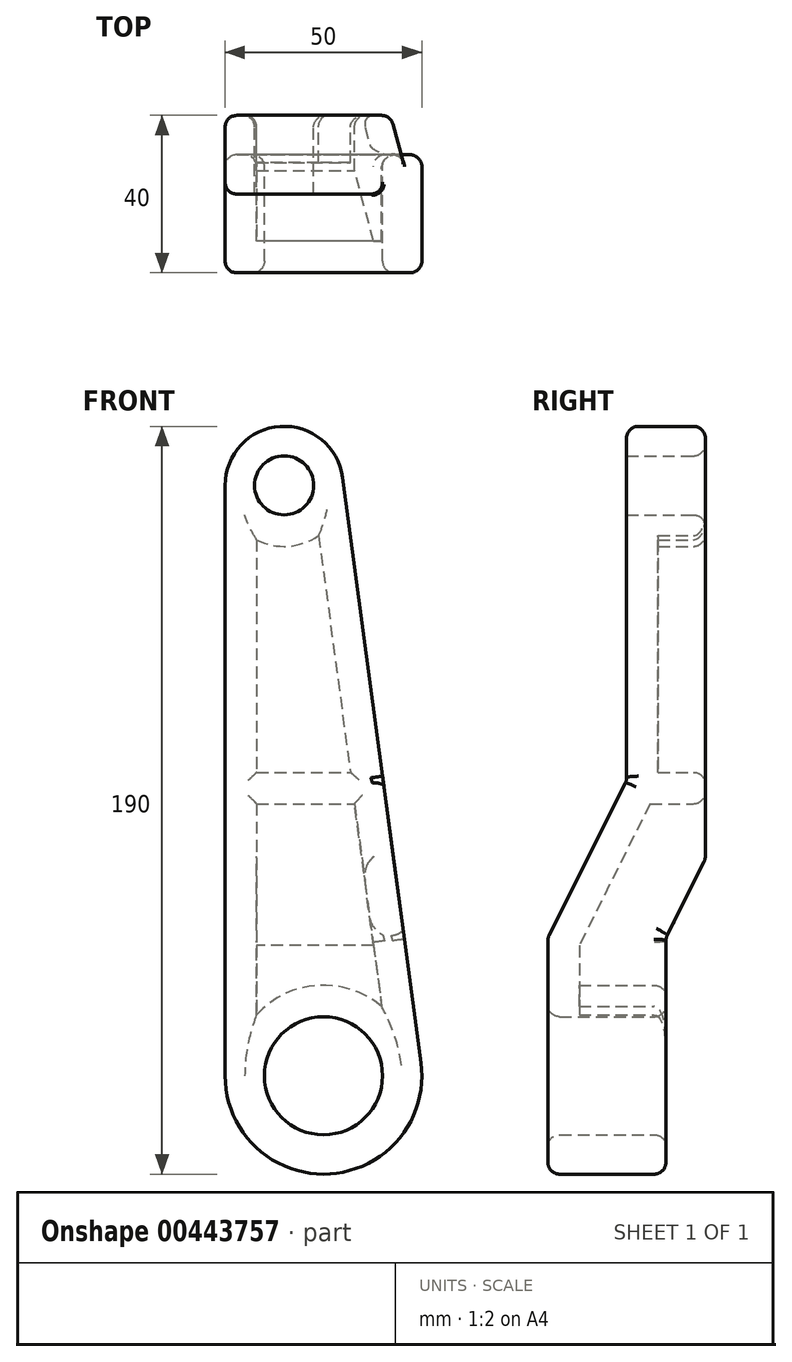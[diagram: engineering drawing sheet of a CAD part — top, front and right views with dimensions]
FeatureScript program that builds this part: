
annotation { "Feature Type Name" : "Feature", "Feature Type Description" : "" }
export const myFeature = defineFeature(function(context is Context, id is Id, definition is map)
    precondition{}
    {
        {
            var Q0;
            Q0=qCreatedBy(makeId("Front.planeOp"),FACE);
            var sketch = newSketch(context, id + "F0", { "sketchPlane" : qUnion([Q0])});
            skArc(sketch, "E0", {"start": v(-25, 0) * mm, "mid": v(1.66, -24.94) * mm, "end": v(24.78, 3.32) * mm});
            skLineSegment(sketch, "E1", {"start": v(-25, 150) * mm, "end": v(-25, 0) * mm});
            skArc(sketch, "E2", {"start": v(4.87, 152) * mm, "mid": v(-11, 164.97) * mm, "end": v(-25, 150) * mm});
            skLineSegment(sketch, "E3", {"start": v(4.87, 152) * mm, "end": v(24.78, 3.32) * mm});
            skSolve(sketch);
        }
        {
            var Q0;
            Q0 = qSketchRegion(id + "F0", true);
            extrude(context, id + "F1", {"entities" : qUnion([Q0]), "depth" : 40 * mm});
        }
        {
            var Q0;
            Q0=makeQuery(id+"F1.opExtrude","SWEPT_FACE",FACE,{"disambiguationData":[OSD([sQuery(id+"F0.wireOp",EDGE,"E1")])]});
            var sketch = newSketch(context, id + "F2", { "sketchPlane" : qUnion([Q0])});
            skLineSegment(sketch, "E4", {"start": v(0, 55) * mm, "end": v(0, -25.94) * mm});
            skLineSegment(sketch, "E5", {"start": v(10, -25.94) * mm, "end": v(10, 35) * mm});
            skLineSegment(sketch, "E6", {"start": v(10, 35) * mm, "end": v(0, 55) * mm});
            skLineSegment(sketch, "E7", {"start": v(40, 35) * mm, "end": v(40, 165.97) * mm});
            skLineSegment(sketch, "E8", {"start": v(20, 165.97) * mm, "end": v(20, 75) * mm});
            skLineSegment(sketch, "E9", {"start": v(20, 75) * mm, "end": v(40, 35) * mm});
            skLineSegment(sketch, "E10", {"start": v(0, -25.94) * mm, "end": v(10, -25.94) * mm});
            skLineSegment(sketch, "E11", {"start": v(20, 165.97) * mm, "end": v(40, 165.97) * mm});
            skSolve(sketch);
        }
        {
            var Q0;
            Q0 = qSketchRegion(id + "F2", true);
            extrude(context, id + "F3", {"entities" : qUnion([Q0]), "operationType" : NewBodyOperationType.REMOVE, "endBound" : BoundingType.THROUGH_ALL, "oppositeDirection" : true, "depth" : 25 * mm});
        }
        {
            var Q0;
            Q0=makeQuery(id+"F1.opExtrude","CAP_FACE",FACE,{"disambiguationData":[OSD([sQuery(id+"F0.wireOp",EDGE,"E0"),sQuery(id+"F0.wireOp",EDGE,"E1"),sQuery(id+"F0.wireOp",EDGE,"E2"),sQuery(id+"F0.wireOp",EDGE,"E3")])],"isStart":true});
            var sketch = newSketch(context, id + "F4", { "sketchPlane" : qUnion([Q0])});
            skCircle(sketch, "E12", {"center": v(10, 150) * mm, "radius": 7.5 * mm});
            skCircle(sketch, "E13", {"center": v(0, 0) * mm, "radius": 15 * mm});
            skSolve(sketch);
        }
        {
            var Q0;
            Q0 = qSketchRegion(id + "F4", true);
            extrude(context, id + "F5", {"entities" : qUnion([Q0]), "operationType" : NewBodyOperationType.REMOVE, "endBound" : BoundingType.THROUGH_ALL, "oppositeDirection" : true, "depth" : 25 * mm});
        }
        {
            var Q0;
            Q0=makeQuery(id+"F5.boolean.opBoolean","SPLIT",FACE,{"disambiguationData":[TD([makeQuery(id+"F1.opExtrude","SWEPT_FACE",FACE,{"disambiguationData":[OSD([sQuery(id+"F0.wireOp",EDGE,"E0")])]})])],"derivedFrom":makeQuery(id+"F3.boolean.opBoolean","COPY",FACE,{"derivedFrom":makeQuery(id+"F3.opExtrude","SWEPT_FACE",FACE,{"disambiguationData":[OSD([sQuery(id+"F2.wireOp",EDGE,"E5")])]})})});
            var Q1;
            Q1=makeQuery(id+"F3.boolean.opBoolean","COPY",FACE,{"derivedFrom":makeQuery(id+"F3.opExtrude","SWEPT_FACE",FACE,{"disambiguationData":[OSD([sQuery(id+"F2.wireOp",EDGE,"E6")])]})});
            var Q2;
            Q2=makeQuery(id+"F1.opExtrude","CAP_FACE",FACE,{"disambiguationData":[OSD([sQuery(id+"F0.wireOp",EDGE,"E0"),sQuery(id+"F0.wireOp",EDGE,"E1"),sQuery(id+"F0.wireOp",EDGE,"E2"),sQuery(id+"F0.wireOp",EDGE,"E3")])],"isStart":true});
            shell(context, id + "F6", {"entities" : qUnion([Q0, Q1, Q2]), "thickness" : 8 * mm});
        }
        {
            var Q0;
            Q0=makeQuery(id+"F1.opExtrude","CAP_FACE",FACE,{"disambiguationData":[OSD([sQuery(id+"F0.wireOp",EDGE,"E0"),sQuery(id+"F0.wireOp",EDGE,"E1"),sQuery(id+"F0.wireOp",EDGE,"E2"),sQuery(id+"F0.wireOp",EDGE,"E3")])],"isStart":true});
            var sketch = newSketch(context, id + "F7", { "sketchPlane" : qUnion([Q0])});
            skLineSegment(sketch, "E14", {"start": v(-6.82, 77.11) * mm, "end": v(17, 77.11) * mm});
            skLineSegment(sketch, "E15", {"start": v(-7.9, 69.11) * mm, "end": v(17, 69.11) * mm});
            skLineSegment(sketch, "E16.0", {"start": v(-6.82, 77.11) * mm, "end": v(-7.9, 69.11) * mm});
            skLineSegment(sketch, "E17.0", {"start": v(17, 77.11) * mm, "end": v(17, 69.11) * mm});
            skPoint(sketch, "E18.orphan", {"position": v(1.23, 137.22) * mm});
            skPoint(sketch, "E19.orphan", {"position": v(17, 136.17) * mm});
            skPoint(sketch, "E20.orphan", {"position": v(17, 55) * mm});
            skPoint(sketch, "E21.orphan", {"position": v(-9.79, 55) * mm});
            skSolve(sketch);
        }
        {
            var Q0;
            Q0 = qSketchRegion(id + "F7", true);
            extrude(context, id + "F8", {"entities" : qUnion([Q0]), "operationType" : NewBodyOperationType.ADD, "endBound" : BoundingType.UP_TO_NEXT, "oppositeDirection" : true, "depth" : 25 * mm});
        }
        {
            var Q0;
            Q0=makeQuery(id+"F3.boolean.opBoolean","COPY",FACE,{"derivedFrom":makeQuery(id+"F3.opExtrude","SWEPT_FACE",FACE,{"disambiguationData":[OSD([sQuery(id+"F2.wireOp",EDGE,"E5")])]})});
            var Q1;
            Q1=makeQuery(id+"F3.boolean.opBoolean","COPY",FACE,{"derivedFrom":makeQuery(id+"F3.opExtrude","SWEPT_FACE",FACE,{"disambiguationData":[OSD([sQuery(id+"F2.wireOp",EDGE,"E6")])]})});
            var Q2;
            Q2=makeQuery(id+"F1.opExtrude","CAP_FACE",FACE,{"disambiguationData":[OSD([sQuery(id+"F0.wireOp",EDGE,"E0"),sQuery(id+"F0.wireOp",EDGE,"E1"),sQuery(id+"F0.wireOp",EDGE,"E2"),sQuery(id+"F0.wireOp",EDGE,"E3")])],"isStart":true});
            var Q3;
            Q3=makeQuery(id+"F8.opExtrude","CAP_FACE",FACE,{"disambiguationData":[OSD([sQuery(id+"F7.wireOp",EDGE,"E14"),sQuery(id+"F7.wireOp",EDGE,"E15"),sQuery(id+"F7.wireOp",EDGE,"E16.0"),sQuery(id+"F7.wireOp",EDGE,"E17.0")])],"isStart":true});
            var Q4;
            Q4=makeQuery(id+"F1.opExtrude","SWEPT_FACE",FACE,{"disambiguationData":[OSD([sQuery(id+"F0.wireOp",EDGE,"E0")])]});
            var Q5;
            Q5=makeQuery(id+"F1.opExtrude","CAP_FACE",FACE,{"disambiguationData":[OSD([sQuery(id+"F0.wireOp",EDGE,"E0"),sQuery(id+"F0.wireOp",EDGE,"E1"),sQuery(id+"F0.wireOp",EDGE,"E2"),sQuery(id+"F0.wireOp",EDGE,"E3")])],"isStart":false});
            var Q6;
            Q6=makeQuery(id+"F3.boolean.opBoolean","COPY",FACE,{"derivedFrom":makeQuery(id+"F3.opExtrude","SWEPT_FACE",FACE,{"disambiguationData":[OSD([sQuery(id+"F2.wireOp",EDGE,"E9")])]})});
            var Q7;
            Q7=makeQuery(id+"F1.opExtrude","SWEPT_FACE",FACE,{"disambiguationData":[OSD([sQuery(id+"F0.wireOp",EDGE,"E3")])]});
            var Q8;
            Q8=makeQuery(id+"F1.opExtrude","SWEPT_FACE",FACE,{"disambiguationData":[OSD([sQuery(id+"F0.wireOp",EDGE,"E2")])]});
            fillet(context, id + "F9", {"entities" : qUnion([Q0, Q1, Q2, Q3, Q4, Q5, Q6, Q7, Q8]), "radius" : 3 * mm, "tangentPropagation" : true, "allowEdgeOverflow" : false});
        }
    });
